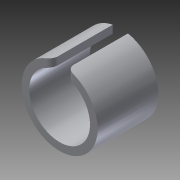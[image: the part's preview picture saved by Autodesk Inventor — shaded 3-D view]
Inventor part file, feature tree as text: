
AUTODESK INVENTOR PART (.ipt)
format: ipt  version: 2013 (Build 170138000, 138)  size: 102,912 bytes
history: native  units: in
note: dims shown in document units (in); Inventor stores cm internally (conversion verified against a paired STEP export)
features: extrude x1, fillet x1, sketch x1
ambient origin geometry x8: Origin, YZ Plane, XZ Plane, XY Plane, X Axis, Y Axis, Z Axis, Center Point
bodies: Solid1 (feature_tree)
feature tree (3):
  extrude  "Extrusion1"  Depth=0.625in
  fillet  "Fillet1"  Radius=0.5in
  sketch  "Sketch1"  dims[d0=0.5in d1=0.625in d2=0.5in d3=0.0in d4=0.0625in d5=0.0625in d6=0.05in]
